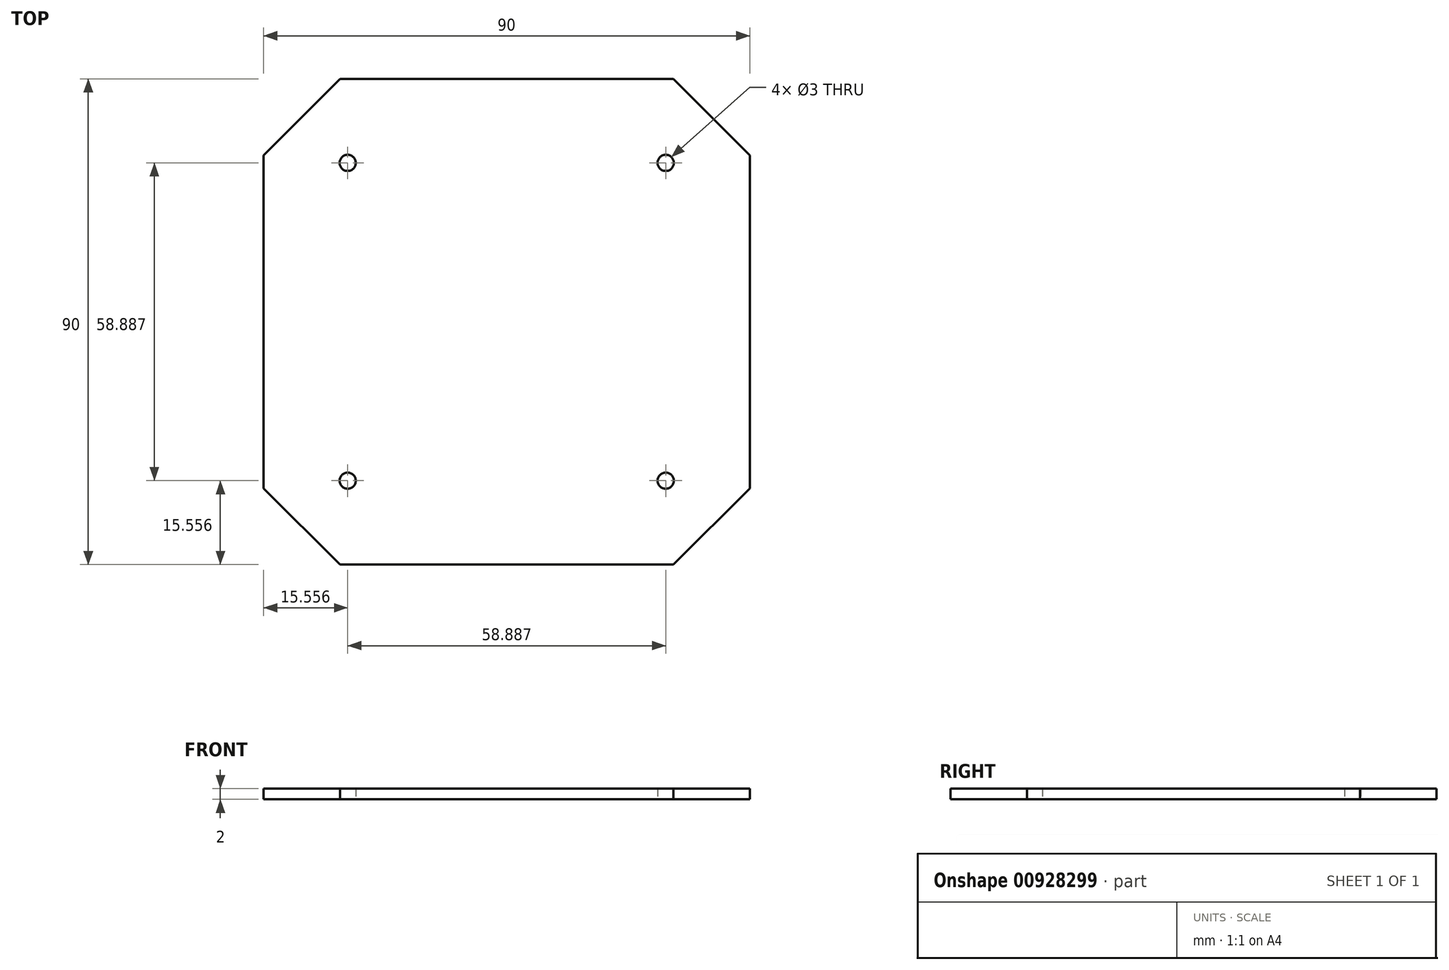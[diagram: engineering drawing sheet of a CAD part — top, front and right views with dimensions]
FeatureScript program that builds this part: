
annotation { "Feature Type Name" : "Feature", "Feature Type Description" : "" }
export const myFeature = defineFeature(function(context is Context, id is Id, definition is map)
    precondition{}
    {
        {
            var Q0;
            Q0=qCreatedBy(makeId("Top.planeOp"),FACE);
            var sketch = newSketch(context, id + "F0", { "sketchPlane" : qUnion([Q0])});
            skLineSegment(sketch, "E0.bottom", {"start": v(30.86, -45) * mm, "end": v(-30.86, -45) * mm});
            skLineSegment(sketch, "E0.top", {"start": v(30.86, 45) * mm, "end": v(-30.86, 45) * mm});
            skLineSegment(sketch, "E0.left", {"start": v(45, -30.86) * mm, "end": v(45, 30.86) * mm});
            skLineSegment(sketch, "E0.right", {"start": v(-45, -30.86) * mm, "end": v(-45, 30.86) * mm});
            skPoint(sketch, "E0.middle", {"position": v(0, 0) * mm});
            skCircle(sketch, "E1.cCircle", {"center": v(0, 0) * mm, "radius": 10 * mm, "construction": true});
            skLineSegment(sketch, "E1.0", {"start": v(-1.27, -12.87) * mm, "end": v(-12.87, -1.27) * mm});
            skLineSegment(sketch, "E1.1", {"start": v(-12.87, 1.27) * mm, "end": v(-1.27, 12.87) * mm});
            skLineSegment(sketch, "E1.2", {"start": v(1.27, 12.87) * mm, "end": v(12.87, 1.27) * mm});
            skLineSegment(sketch, "E1.3", {"start": v(12.87, -1.27) * mm, "end": v(1.27, -12.87) * mm});
            skPoint(sketch, "E1.0.midPoint", {"position": v(-7.07, -7.07) * mm});
            skLineSegment(sketch, "E2", {"start": v(-30.86, 45) * mm, "end": v(-45, 30.86) * mm});
            skLineSegment(sketch, "E3", {"start": v(45, -30.86) * mm, "end": v(30.86, -45) * mm});
            skLineSegment(sketch, "E4", {"start": v(-45, -30.86) * mm, "end": v(-30.86, -45) * mm});
            skLineSegment(sketch, "E5", {"start": v(30.86, 45) * mm, "end": v(45, 30.86) * mm});
            skPoint(sketch, "E6.orphan", {"position": v(-45, 45) * mm});
            skPoint(sketch, "E7.orphan", {"position": v(45, 45) * mm});
            skPoint(sketch, "E8.orphan", {"position": v(45, -45) * mm});
            skPoint(sketch, "E9.orphan", {"position": v(-45, -45) * mm});
            skLineSegment(sketch, "E10", {"start": v(-49.5, -49.5) * mm, "end": v(0, 0) * mm});
            skLineSegment(sketch, "E11", {"start": v(0, 0) * mm, "end": v(49.5, 49.5) * mm});
            skLineSegment(sketch, "E12", {"start": v(0, 0) * mm, "end": v(-49.5, 49.5) * mm});
            skLineSegment(sketch, "E13", {"start": v(0, 0) * mm, "end": v(49.5, -49.5) * mm});
            skLineSegment(sketch, "E14", {"start": v(-1.27, 12.87) * mm, "end": v(-32.13, 43.73) * mm});
            skLineSegment(sketch, "E15", {"start": v(-12.87, 1.27) * mm, "end": v(-43.73, 32.13) * mm});
            skLineSegment(sketch, "E16", {"start": v(1.27, 12.87) * mm, "end": v(32.13, 43.73) * mm});
            skLineSegment(sketch, "E17", {"start": v(12.87, 1.27) * mm, "end": v(43.73, 32.13) * mm});
            skLineSegment(sketch, "E18", {"start": v(12.87, -1.27) * mm, "end": v(43.73, -32.13) * mm});
            skLineSegment(sketch, "E19", {"start": v(1.27, -12.87) * mm, "end": v(32.13, -43.73) * mm});
            skLineSegment(sketch, "E20", {"start": v(-12.87, -1.27) * mm, "end": v(-43.73, -32.13) * mm});
            skLineSegment(sketch, "E21", {"start": v(-1.27, -12.87) * mm, "end": v(-32.13, -43.73) * mm});
            skLineSegment(sketch, "E22", {"start": v(-14.14, 0) * mm, "end": v(-45, -30.86) * mm});
            skLineSegment(sketch, "E23", {"start": v(-14.14, 0) * mm, "end": v(-45, 30.86) * mm});
            skLineSegment(sketch, "E24", {"start": v(30.86, 45) * mm, "end": v(0, 14.14) * mm});
            skLineSegment(sketch, "E25", {"start": v(45, 30.86) * mm, "end": v(14.14, 0) * mm});
            skLineSegment(sketch, "E26", {"start": v(14.14, 0) * mm, "end": v(45, -30.86) * mm});
            skLineSegment(sketch, "E27", {"start": v(0, -14.14) * mm, "end": v(30.86, -45) * mm});
            skLineSegment(sketch, "E28", {"start": v(0, -14.14) * mm, "end": v(-30.86, -45) * mm});
            skLineSegment(sketch, "E29", {"start": v(0, 14.14) * mm, "end": v(-30.86, 45) * mm});
            skLineSegment(sketch, "E30", {"start": v(0, 11.6) * mm, "end": v(-11.6, 0) * mm});
            skLineSegment(sketch, "E31", {"start": v(-11.6, 0) * mm, "end": v(0, -11.6) * mm});
            skLineSegment(sketch, "E32", {"start": v(0, 11.6) * mm, "end": v(11.6, 0) * mm});
            skLineSegment(sketch, "E33", {"start": v(11.6, 0) * mm, "end": v(0, -11.6) * mm});
            skLineSegment(sketch, "E34.bottom", {"start": v(-30.86, -45) * mm, "end": v(30.86, -45) * mm});
            skLineSegment(sketch, "E34.top", {"start": v(-20.86, -100) * mm, "end": v(20.86, -100) * mm});
            skLineSegment(sketch, "E34.left", {"start": v(-30.86, -45) * mm, "end": v(-30.86, -90) * mm});
            skLineSegment(sketch, "E34.right", {"start": v(30.86, -45) * mm, "end": v(30.86, -90) * mm});
            skLineSegment(sketch, "E35.bottom", {"start": v(-30.86, 45) * mm, "end": v(30.86, 45) * mm});
            skLineSegment(sketch, "E35.top", {"start": v(-20.86, 100) * mm, "end": v(20.86, 100) * mm});
            skLineSegment(sketch, "E35.left", {"start": v(-30.86, 45) * mm, "end": v(-30.86, 90) * mm});
            skLineSegment(sketch, "E35.right", {"start": v(30.86, 45) * mm, "end": v(30.86, 90) * mm});
            skPoint(sketch, "E36.visualSharp", {"position": v(-30.86, 100) * mm});
            skArc(sketch, "E36.filletArc", {"start": v(-20.86, 100) * mm, "mid": v(-27.93, 97.07) * mm, "end": v(-30.86, 90) * mm});
            skPoint(sketch, "E37.visualSharp", {"position": v(30.86, 100) * mm});
            skArc(sketch, "E37.filletArc", {"start": v(30.86, 90) * mm, "mid": v(27.93, 97.07) * mm, "end": v(20.86, 100) * mm});
            skPoint(sketch, "E38.visualSharp", {"position": v(-30.86, -100) * mm});
            skArc(sketch, "E38.filletArc", {"start": v(-30.86, -90) * mm, "mid": v(-27.93, -97.07) * mm, "end": v(-20.86, -100) * mm});
            skPoint(sketch, "E39.visualSharp", {"position": v(30.86, -100) * mm});
            skArc(sketch, "E39.filletArc", {"start": v(20.86, -100) * mm, "mid": v(27.93, -97.07) * mm, "end": v(30.86, -90) * mm});
            skCircle(sketch, "E40", {"center": v(-29.44, -29.44) * mm, "radius": 1.5 * mm});
            skCircle(sketch, "E41", {"center": v(29.44, -29.44) * mm, "radius": 1.5 * mm});
            skCircle(sketch, "E42", {"center": v(-29.44, 29.44) * mm, "radius": 1.5 * mm});
            skCircle(sketch, "E43", {"center": v(29.44, 29.44) * mm, "radius": 1.5 * mm});
            skSolve(sketch);
        }
        {
            var Q0;
            {var subQ5=sQuery(id+"F0.wireOp",EDGE,"E18");Q0=makeQuery(id+"F0.imprint","IMPRINT",FACE,{"disambiguationData":[TD([[makeQuery(id+"F0.imprint","IMPRINT",EDGE,{"derivedFrom":subQ5}),-1.0]])]});}
            var Q1;
            {var subQ5=sQuery(id+"F0.wireOp",EDGE,"E20");Q1=makeQuery(id+"F0.imprint","IMPRINT",FACE,{"disambiguationData":[TD([[makeQuery(id+"F0.imprint","IMPRINT",EDGE,{"derivedFrom":subQ5}),1.0]])]});}
            var Q2;
            Q2=makeQuery(id+"F0.imprint","IMPRINT",FACE,{"disambiguationData":[TD([[makeQuery(id+"F0.imprint","IMPRINT",EDGE,{"derivedFrom":sQuery(id+"F0.wireOp",EDGE,"E0.left")}),1.0]])]});
            var Q3;
            {var subQ4=sQuery(id+"F0.wireOp",EDGE,"E14");Q3=makeQuery(id+"F0.imprint","IMPRINT",FACE,{"disambiguationData":[TD([[makeQuery(id+"F0.imprint","IMPRINT",EDGE,{"derivedFrom":subQ4}),-1.0]])]});}
            var Q4;
            {var subQ5=sQuery(id+"F0.wireOp",EDGE,"E14");Q4=makeQuery(id+"F0.imprint","IMPRINT",FACE,{"disambiguationData":[TD([[makeQuery(id+"F0.imprint","IMPRINT",EDGE,{"derivedFrom":subQ5}),1.0]])]});}
            var Q5;
            {var subQ3=sQuery(id+"F0.wireOp",EDGE,"E32");var subQ5=sQuery(id+"F0.wireOp",EDGE,"E30");var subQ7=makeQuery(id+"F0.imprint","INTERSECT",VERTEX,{"derivedFrom":[subQ5,subQ3]});Q5=makeQuery(id+"F0.imprint","IMPRINT",FACE,{"disambiguationData":[TD([[makeQuery(id+"F0.imprint","IMPRINT",EDGE,{"disambiguationData":[TD([[subQ7,-1.0]])],"derivedFrom":subQ5}),1.0]])]});}
            var Q6;
            Q6=makeQuery(id+"F0.imprint","IMPRINT",FACE,{"disambiguationData":[TD([[makeQuery(id+"F0.imprint","IMPRINT",EDGE,{"derivedFrom":sQuery(id+"F0.wireOp",EDGE,"E27")}),-1.0]])]});
            var Q7;
            {var subQ2=sQuery(id+"F0.wireOp",EDGE,"E19");Q7=makeQuery(id+"F0.imprint","IMPRINT",FACE,{"disambiguationData":[TD([[makeQuery(id+"F0.imprint","IMPRINT",EDGE,{"derivedFrom":subQ2}),-1.0]])]});}
            var Q8;
            {var subQ8=sQuery(id+"F0.wireOp",EDGE,"E21");Q8=makeQuery(id+"F0.imprint","IMPRINT",FACE,{"disambiguationData":[TD([[makeQuery(id+"F0.imprint","IMPRINT",EDGE,{"derivedFrom":subQ8}),-1.0]])]});}
            var Q9;
            {var subQ8=sQuery(id+"F0.wireOp",EDGE,"E15");Q9=makeQuery(id+"F0.imprint","IMPRINT",FACE,{"disambiguationData":[TD([[makeQuery(id+"F0.imprint","IMPRINT",EDGE,{"derivedFrom":subQ8}),-1.0]])]});}
            var Q10;
            Q10=makeQuery(id+"F0.imprint","IMPRINT",FACE,{"disambiguationData":[TD([[makeQuery(id+"F0.imprint","IMPRINT",EDGE,{"derivedFrom":sQuery(id+"F0.wireOp",EDGE,"E0.right")}),-1.0]])]});
            var Q11;
            Q11=makeQuery(id+"F0.imprint","IMPRINT",FACE,{"disambiguationData":[TD([[makeQuery(id+"F0.imprint","IMPRINT",EDGE,{"derivedFrom":sQuery(id+"F0.wireOp",EDGE,"E34.bottom")}),-1.0]])]});
            var Q12;
            {var subQ3=sQuery(id+"F0.wireOp",EDGE,"E32");var subQ5=sQuery(id+"F0.wireOp",EDGE,"E33");var subQ7=makeQuery(id+"F0.imprint","INTERSECT",VERTEX,{"derivedFrom":[subQ3,subQ5]});Q12=makeQuery(id+"F0.imprint","IMPRINT",FACE,{"disambiguationData":[TD([[makeQuery(id+"F0.imprint","IMPRINT",EDGE,{"disambiguationData":[TD([[subQ7,1.0]])],"derivedFrom":subQ3}),-1.0]])]});}
            var Q13;
            {var subQ3=sQuery(id+"F0.wireOp",EDGE,"E31");var subQ5=sQuery(id+"F0.wireOp",EDGE,"E33");var subQ6=makeQuery(id+"F0.imprint","INTERSECT",VERTEX,{"derivedFrom":[subQ3,subQ5]});Q13=makeQuery(id+"F0.imprint","IMPRINT",FACE,{"disambiguationData":[TD([[makeQuery(id+"F0.imprint","IMPRINT",EDGE,{"disambiguationData":[TD([[subQ6,1.0]])],"derivedFrom":subQ3}),1.0]])]});}
            var Q14;
            {var subQ8=sQuery(id+"F0.wireOp",EDGE,"E15");Q14=makeQuery(id+"F0.imprint","IMPRINT",FACE,{"disambiguationData":[TD([[makeQuery(id+"F0.imprint","IMPRINT",EDGE,{"derivedFrom":subQ8}),1.0]])]});}
            var Q15;
            {var subQ8=sQuery(id+"F0.wireOp",EDGE,"E16");Q15=makeQuery(id+"F0.imprint","IMPRINT",FACE,{"disambiguationData":[TD([[makeQuery(id+"F0.imprint","IMPRINT",EDGE,{"derivedFrom":subQ8}),-1.0]])]});}
            var Q16;
            {var subQ5=sQuery(id+"F0.wireOp",EDGE,"E17");Q16=makeQuery(id+"F0.imprint","IMPRINT",FACE,{"disambiguationData":[TD([[makeQuery(id+"F0.imprint","IMPRINT",EDGE,{"derivedFrom":subQ5}),1.0]])]});}
            var Q17;
            Q17=makeQuery(id+"F0.imprint","IMPRINT",FACE,{"disambiguationData":[TD([[makeQuery(id+"F0.imprint","IMPRINT",EDGE,{"derivedFrom":sQuery(id+"F0.wireOp",EDGE,"E24")}),-1.0]])]});
            var Q18;
            {var subQ3=sQuery(id+"F0.wireOp",EDGE,"E31");var subQ5=sQuery(id+"F0.wireOp",EDGE,"E30");var subQ7=makeQuery(id+"F0.imprint","INTERSECT",VERTEX,{"derivedFrom":[subQ5,subQ3]});Q18=makeQuery(id+"F0.imprint","IMPRINT",FACE,{"disambiguationData":[TD([[makeQuery(id+"F0.imprint","IMPRINT",EDGE,{"disambiguationData":[TD([[subQ7,1.0]])],"derivedFrom":subQ5}),1.0]])]});}
            var Q19;
            {var subQ2=sQuery(id+"F0.wireOp",EDGE,"E17");Q19=makeQuery(id+"F0.imprint","IMPRINT",FACE,{"disambiguationData":[TD([[makeQuery(id+"F0.imprint","IMPRINT",EDGE,{"derivedFrom":subQ2}),-1.0]])]});}
            var Q20;
            Q20=makeQuery(id+"F0.imprint","IMPRINT",FACE,{"disambiguationData":[TD([[makeQuery(id+"F0.imprint","IMPRINT",EDGE,{"derivedFrom":sQuery(id+"F0.wireOp",EDGE,"E35.bottom")}),1.0]])]});
            var Q21;
            {var subQ8=sQuery(id+"F0.wireOp",EDGE,"E19");Q21=makeQuery(id+"F0.imprint","IMPRINT",FACE,{"disambiguationData":[TD([[makeQuery(id+"F0.imprint","IMPRINT",EDGE,{"derivedFrom":subQ8}),1.0]])]});}
            extrude(context, id + "F1", {"entities" : qUnion([Q0, Q1, Q2, Q3, Q4, Q5, Q6, Q7, Q8, Q9, Q10, Q11, Q12, Q13, Q14, Q15, Q16, Q17, Q18, Q19, Q20, Q21]), "depth" : 2 * mm, "offsetDistance" : 25 * mm});
        }
    });
